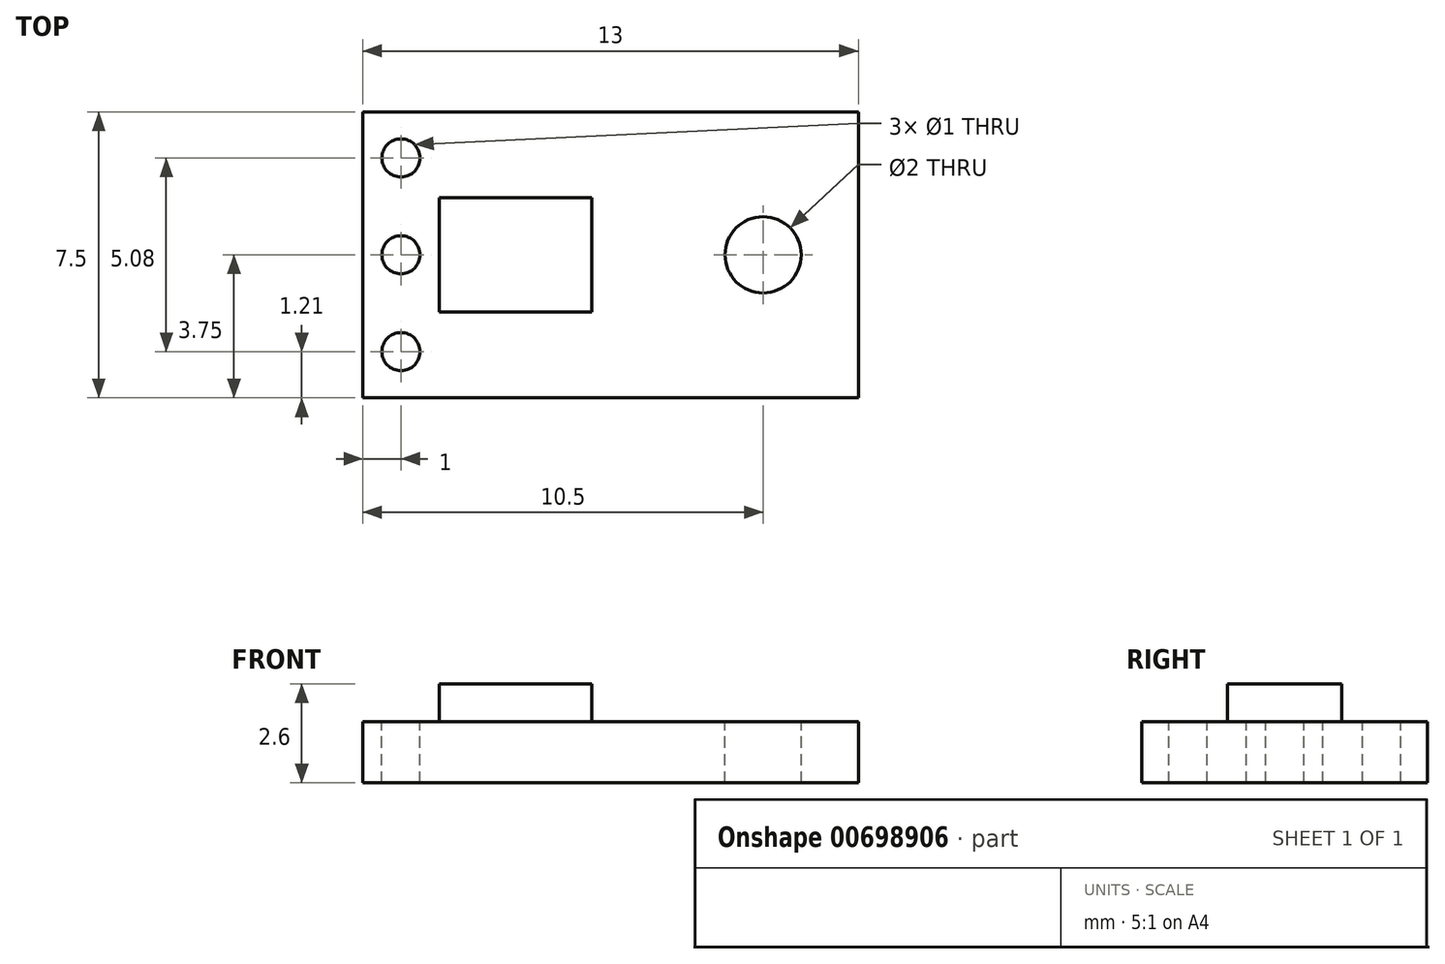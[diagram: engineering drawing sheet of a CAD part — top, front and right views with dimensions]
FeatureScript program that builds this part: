
annotation { "Feature Type Name" : "Feature", "Feature Type Description" : "" }
export const myFeature = defineFeature(function(context is Context, id is Id, definition is map)
    precondition{}
    {
        {
            var Q0;
            Q0=qCreatedBy(makeId("Top.planeOp"),FACE);
            var sketch = newSketch(context, id + "F0", { "sketchPlane" : qUnion([Q0])});
            skLineSegment(sketch, "E0.bottom", {"start": v(6.5, 3.75) * mm, "end": v(-6.5, 3.75) * mm});
            skLineSegment(sketch, "E0.top", {"start": v(6.5, -3.75) * mm, "end": v(-6.5, -3.75) * mm});
            skLineSegment(sketch, "E0.left", {"start": v(6.5, 3.75) * mm, "end": v(6.5, -3.75) * mm});
            skLineSegment(sketch, "E0.right", {"start": v(-6.5, 3.75) * mm, "end": v(-6.5, -3.75) * mm});
            skPoint(sketch, "E0.middle", {"position": v(0, 0) * mm});
            skLineSegment(sketch, "E1.bottom", {"start": v(-0.5, 1.5) * mm, "end": v(-4.5, 1.5) * mm});
            skLineSegment(sketch, "E1.top", {"start": v(-0.5, -1.5) * mm, "end": v(-4.5, -1.5) * mm});
            skLineSegment(sketch, "E1.left", {"start": v(-0.5, 1.5) * mm, "end": v(-0.5, -1.5) * mm});
            skLineSegment(sketch, "E1.right", {"start": v(-4.5, 1.5) * mm, "end": v(-4.5, -1.5) * mm});
            skPoint(sketch, "E1.middle", {"position": v(-2.5, 0) * mm});
            skCircle(sketch, "E2", {"center": v(4, 0) * mm, "radius": 1 * mm});
            skCircle(sketch, "E3", {"center": v(-5.5, 2.54) * mm, "radius": 0.5 * mm});
            skCircle(sketch, "E4", {"center": v(-5.5, 0) * mm, "radius": 0.5 * mm});
            skCircle(sketch, "E5", {"center": v(-5.5, -2.54) * mm, "radius": 0.5 * mm});
            skLineSegment(sketch, "E6", {"start": v(-5.5, 2.54) * mm, "end": v(-5.5, 0) * mm, "construction": true});
            skLineSegment(sketch, "E7", {"start": v(-5.5, 0) * mm, "end": v(-5.5, -2.54) * mm, "construction": true});
            skSolve(sketch);
        }
        {
            var Q0;
            Q0=makeQuery(id+"F0.imprint","IMPRINT",FACE,{"disambiguationData":[TD([[makeQuery(id+"F0.imprint","IMPRINT",EDGE,{"derivedFrom":sQuery(id+"F0.wireOp",EDGE,"E0.bottom")}),1.0]])]});
            var Q1;
            Q1=makeQuery(id+"F0.imprint","IMPRINT",FACE,{"disambiguationData":[TD([[makeQuery(id+"F0.imprint","IMPRINT",EDGE,{"derivedFrom":sQuery(id+"F0.wireOp",EDGE,"E1.bottom")}),1.0]])]});
            extrude(context, id + "F1", {"entities" : qUnion([Q0, Q1]), "oppositeDirection" : true, "depth" : 1.6 * mm});
        }
        {
            var Q0;
            Q0=makeQuery(id+"F0.imprint","IMPRINT",FACE,{"disambiguationData":[TD([[makeQuery(id+"F0.imprint","IMPRINT",EDGE,{"derivedFrom":sQuery(id+"F0.wireOp",EDGE,"E1.bottom")}),1.0]])]});
            extrude(context, id + "F2", {"entities" : qUnion([Q0]), "operationType" : NewBodyOperationType.ADD, "depth" : 1 * mm});
        }
    });
